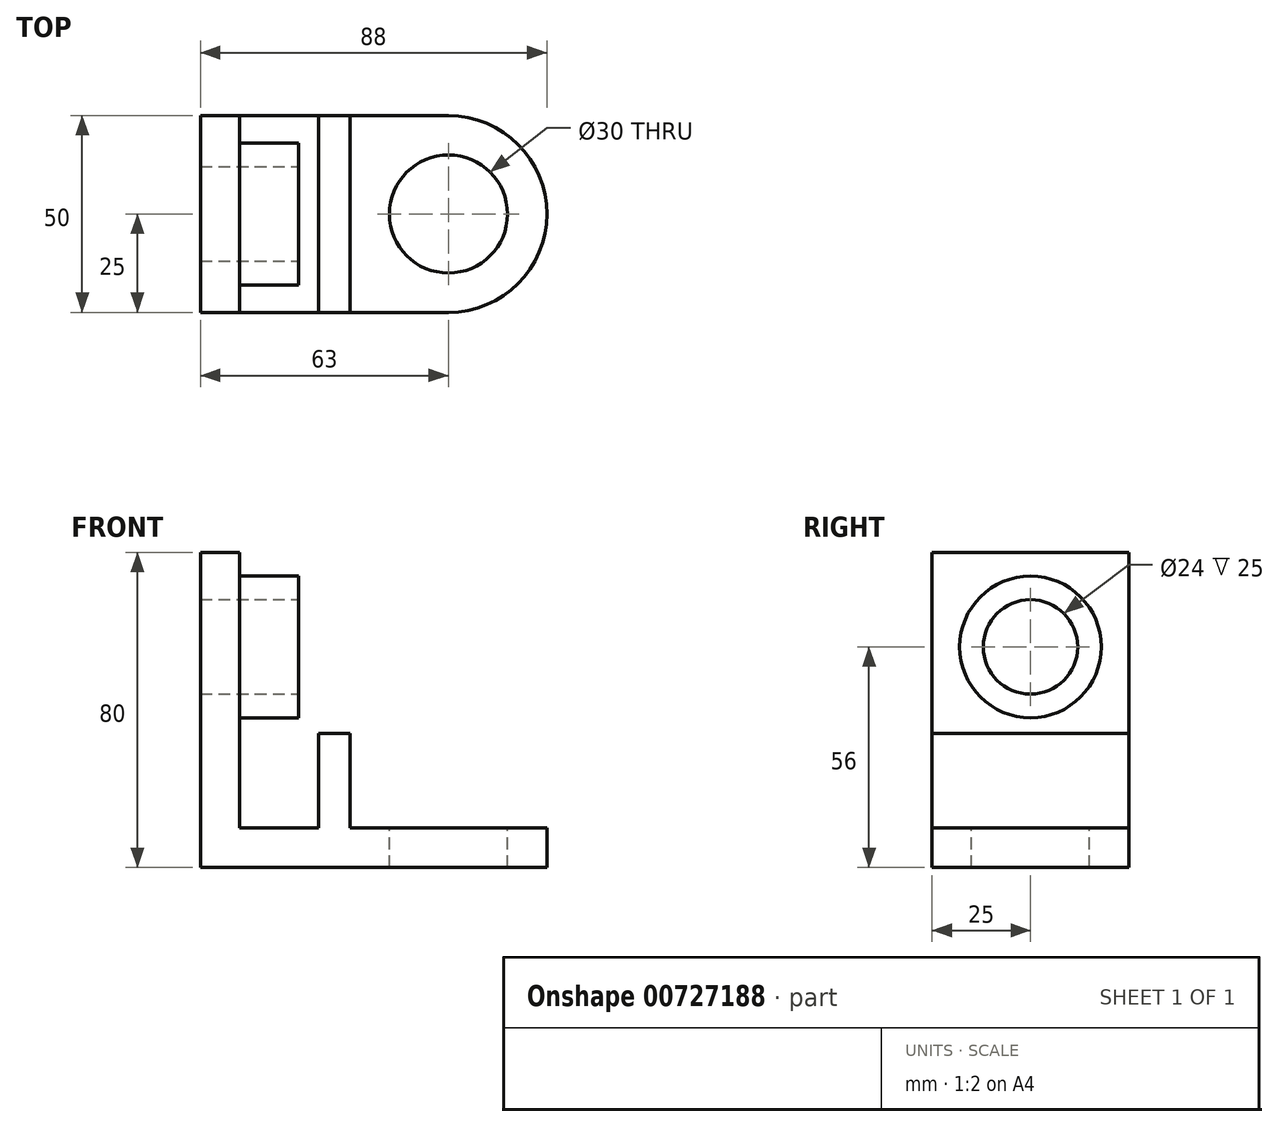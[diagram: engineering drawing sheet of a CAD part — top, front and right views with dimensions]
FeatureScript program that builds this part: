
annotation { "Feature Type Name" : "Feature", "Feature Type Description" : "" }
export const myFeature = defineFeature(function(context is Context, id is Id, definition is map)
    precondition{}
    {
        {
            var Q0;
            Q0=qCreatedBy(makeId("Front.planeOp"),FACE);
            var sketch = newSketch(context, id + "F0", { "sketchPlane" : qUnion([Q0])});
            skLineSegment(sketch, "E0", {"start": v(0, 90) * mm, "end": v(10, 90) * mm});
            skLineSegment(sketch, "E1", {"start": v(0, 0) * mm, "end": v(0, 80) * mm});
            skLineSegment(sketch, "E2", {"start": v(0, 80) * mm, "end": v(10, 80) * mm});
            skLineSegment(sketch, "E3", {"start": v(10, 80) * mm, "end": v(10, 10) * mm});
            skLineSegment(sketch, "E4", {"start": v(10, 10) * mm, "end": v(30, 10) * mm});
            skLineSegment(sketch, "E5", {"start": v(30, 10) * mm, "end": v(30, 34) * mm});
            skLineSegment(sketch, "E6", {"start": v(30, 34) * mm, "end": v(38, 34) * mm});
            skLineSegment(sketch, "E7", {"start": v(38, 34) * mm, "end": v(38, 10) * mm});
            skLineSegment(sketch, "E8", {"start": v(38, 10) * mm, "end": v(88, 10) * mm});
            skLineSegment(sketch, "E9", {"start": v(88, 10) * mm, "end": v(88, 0) * mm});
            skLineSegment(sketch, "E10", {"start": v(88, 0) * mm, "end": v(0, 0) * mm});
            skSolve(sketch);
        }
        {
            var Q0;
            Q0 = qSketchRegion(id + "F0", true);
            extrude(context, id + "F1", {"entities" : qUnion([Q0]), "depth" : 50 * mm, "offsetDistance" : 25 * mm});
        }
        {
            var Q0;
            Q0=makeQuery(id+"F1.opExtrude","CAP_EDGE",EDGE,{"disambiguationData":[OSD([sQuery(id+"F0.wireOp",EDGE,"E9")])],"isStart":false});
            var Q1;
            Q1=makeQuery(id+"F1.opExtrude","CAP_EDGE",EDGE,{"disambiguationData":[OSD([sQuery(id+"F0.wireOp",EDGE,"E9")])],"isStart":true});
            fillet(context, id + "F2", {"entities" : qUnion([Q0, Q1]), "radius" : 25 * mm, "tangentPropagation" : true, "allowEdgeOverflow" : false});
        }
        {
            var Q0;
            Q0=makeQuery(id+"F1.opExtrude","SWEPT_FACE",FACE,{"disambiguationData":[OSD([sQuery(id+"F0.wireOp",EDGE,"E8")])]});
            var sketch = newSketch(context, id + "F3", { "sketchPlane" : qUnion([Q0])});
            skCircle(sketch, "E11", {"center": v(63, -25) * mm, "radius": 15 * mm});
            skSolve(sketch);
        }
        {
            var Q0;
            Q0 = qSketchRegion(id + "F3", true);
            extrude(context, id + "F4", {"entities" : qUnion([Q0]), "operationType" : NewBodyOperationType.REMOVE, "endBound" : BoundingType.UP_TO_NEXT, "oppositeDirection" : true, "depth" : 25 * mm, "offsetDistance" : 25 * mm});
        }
        {
            var Q0;
            Q0=makeQuery(id+"F1.opExtrude","SWEPT_FACE",FACE,{"disambiguationData":[OSD([sQuery(id+"F0.wireOp",EDGE,"E3")])]});
            var sketch = newSketch(context, id + "F5", { "sketchPlane" : qUnion([Q0])});
            skCircle(sketch, "E12", {"center": v(-25, 56) * mm, "radius": 18 * mm});
            skSolve(sketch);
        }
        {
            var Q0;
            Q0=makeQuery(id+"F5.imprint","IMPRINT",FACE,{"disambiguationData":[TD([[makeQuery(id+"F5.imprint","IMPRINT",EDGE,{"derivedFrom":sQuery(id+"F5.wireOp",EDGE,"E12")}),1.0]])]});
            extrude(context, id + "F6", {"entities" : qUnion([Q0]), "operationType" : NewBodyOperationType.ADD, "depth" : 15 * mm, "offsetDistance" : 25 * mm});
        }
        {
            var Q0;
            Q0=makeQuery(id+"F6.opExtrude","CAP_FACE",FACE,{"disambiguationData":[OSD([sQuery(id+"F5.wireOp",EDGE,"E12")])],"isStart":false});
            var sketch = newSketch(context, id + "F7", { "sketchPlane" : qUnion([Q0])});
            skCircle(sketch, "E13", {"center": v(-25, 56) * mm, "radius": 12 * mm});
            skSolve(sketch);
        }
        {
            var Q0;
            Q0 = qSketchRegion(id + "F7", true);
            extrude(context, id + "F8", {"entities" : qUnion([Q0]), "operationType" : NewBodyOperationType.REMOVE, "endBound" : BoundingType.UP_TO_NEXT, "oppositeDirection" : true, "depth" : 25 * mm, "offsetDistance" : 25 * mm});
        }
    });
